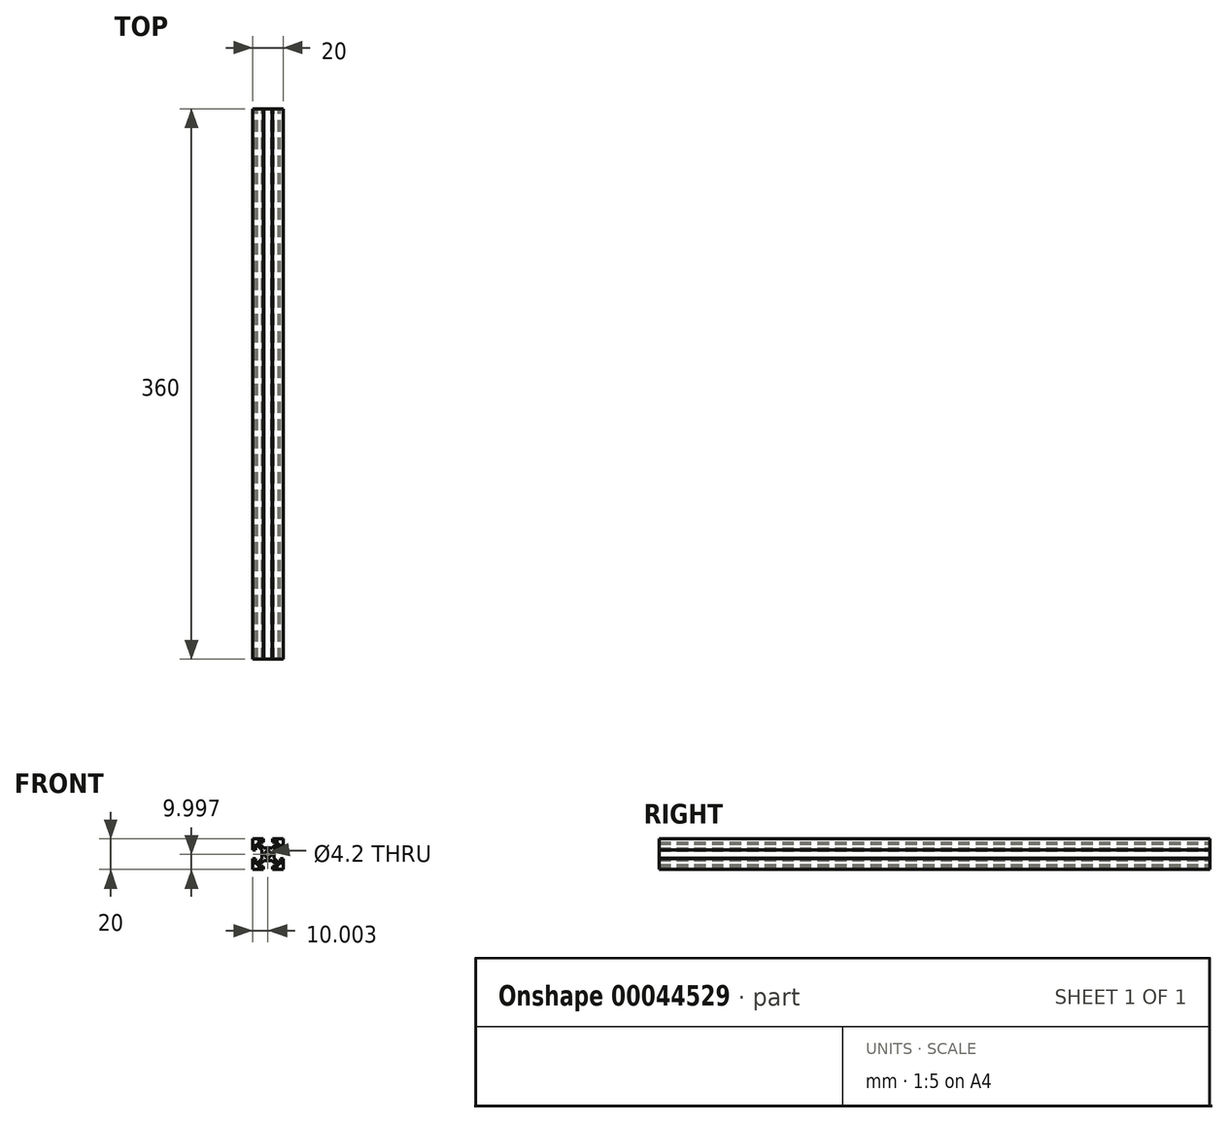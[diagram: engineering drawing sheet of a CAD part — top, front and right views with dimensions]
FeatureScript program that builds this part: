
annotation { "Feature Type Name" : "Feature", "Feature Type Description" : "" }
export const myFeature = defineFeature(function(context is Context, id is Id, definition is map)
    precondition{}
    {
        {
            var Q0;
            Q0=qCreatedBy(makeId("Front.planeOp"),FACE);
            var sketch = newSketch(context, id + "F0", { "sketchPlane" : qUnion([Q0])});
            skLineSegment(sketch, "E0", {"start": v(10.04, -9.96) * mm, "end": v(10.04, -2.96) * mm});
            skLineSegment(sketch, "E1", {"start": v(10.04, 3.04) * mm, "end": v(10.04, 10.04) * mm});
            skLineSegment(sketch, "E2", {"start": v(-6.7, -7.96) * mm, "end": v(-2.7, -3.96) * mm});
            skLineSegment(sketch, "E3", {"start": v(4.04, -2.63) * mm, "end": v(4.04, 2.78) * mm});
            skLineSegment(sketch, "E4", {"start": v(-2.7, -3.96) * mm, "end": v(2.91, -3.96) * mm});
            skLineSegment(sketch, "E5", {"start": v(2.91, -3.96) * mm, "end": v(6.91, -7.96) * mm});
            skLineSegment(sketch, "E6", {"start": v(-2.96, 10.04) * mm, "end": v(-9.96, 10.04) * mm});
            skLineSegment(sketch, "E7", {"start": v(-9.96, 10.04) * mm, "end": v(-9.96, 3.04) * mm});
            skCircle(sketch, "E8", {"center": v(0.04, 0.04) * mm, "radius": 2.1 * mm});
            skLineSegment(sketch, "E9", {"start": v(-7.96, 3.04) * mm, "end": v(-7.96, 6.79) * mm});
            skLineSegment(sketch, "E10", {"start": v(-7.96, 6.79) * mm, "end": v(-3.96, 2.79) * mm});
            skLineSegment(sketch, "E11", {"start": v(-3.96, 2.79) * mm, "end": v(-3.96, -2.71) * mm});
            skLineSegment(sketch, "E12", {"start": v(-3.96, -2.71) * mm, "end": v(-7.96, -6.71) * mm});
            skLineSegment(sketch, "E13", {"start": v(2.9, 4.04) * mm, "end": v(-2.7, 4.04) * mm});
            skLineSegment(sketch, "E14", {"start": v(6.91, -7.96) * mm, "end": v(3.04, -7.96) * mm});
            skLineSegment(sketch, "E15", {"start": v(-7.96, -6.71) * mm, "end": v(-7.96, -2.96) * mm});
            skLineSegment(sketch, "E16", {"start": v(-9.96, -2.96) * mm, "end": v(-9.96, -9.96) * mm});
            skLineSegment(sketch, "E17", {"start": v(-9.96, -9.96) * mm, "end": v(-2.96, -9.96) * mm});
            skLineSegment(sketch, "E18", {"start": v(-2.96, -7.96) * mm, "end": v(-6.7, -7.96) * mm});
            skLineSegment(sketch, "E19", {"start": v(10.04, 10.04) * mm, "end": v(3.04, 10.04) * mm});
            skLineSegment(sketch, "E20", {"start": v(4.04, 2.78) * mm, "end": v(8.04, 6.78) * mm});
            skLineSegment(sketch, "E21", {"start": v(3.04, 8.04) * mm, "end": v(6.91, 8.04) * mm});
            skLineSegment(sketch, "E22", {"start": v(8.04, -2.96) * mm, "end": v(8.04, -6.63) * mm});
            skLineSegment(sketch, "E23", {"start": v(-2.7, 4.04) * mm, "end": v(-6.7, 8.04) * mm});
            skLineSegment(sketch, "E24", {"start": v(8.04, 6.78) * mm, "end": v(8.04, 3.04) * mm});
            skLineSegment(sketch, "E25", {"start": v(6.91, 8.04) * mm, "end": v(2.9, 4.04) * mm});
            skLineSegment(sketch, "E26", {"start": v(8.04, -6.63) * mm, "end": v(4.04, -2.63) * mm});
            skLineSegment(sketch, "E27", {"start": v(-6.7, 8.04) * mm, "end": v(-2.96, 8.04) * mm});
            skLineSegment(sketch, "E28", {"start": v(3.04, -9.96) * mm, "end": v(10.04, -9.96) * mm});
            skLineSegment(sketch, "E29", {"start": v(8.04, 3.04) * mm, "end": v(10.04, 3.04) * mm});
            skLineSegment(sketch, "E30", {"start": v(-2.96, 8.04) * mm, "end": v(-2.96, 10.04) * mm});
            skLineSegment(sketch, "E31", {"start": v(-9.96, 3.04) * mm, "end": v(-7.96, 3.04) * mm});
            skLineSegment(sketch, "E32", {"start": v(3.04, 10.04) * mm, "end": v(3.04, 8.04) * mm});
            skLineSegment(sketch, "E33", {"start": v(10.04, -2.96) * mm, "end": v(8.04, -2.96) * mm});
            skLineSegment(sketch, "E34", {"start": v(-7.96, -2.96) * mm, "end": v(-9.96, -2.96) * mm});
            skLineSegment(sketch, "E35", {"start": v(-2.96, -9.96) * mm, "end": v(-2.96, -7.96) * mm});
            skLineSegment(sketch, "E36", {"start": v(3.04, -7.96) * mm, "end": v(3.04, -9.96) * mm});
            skSolve(sketch);
        }
        {
            var Q0;
            Q0 = qSketchRegion(id + "F0", true);
            extrude(context, id + "F1", {"entities" : qUnion([Q0]), "depth" : 360 * mm});
        }
    });
